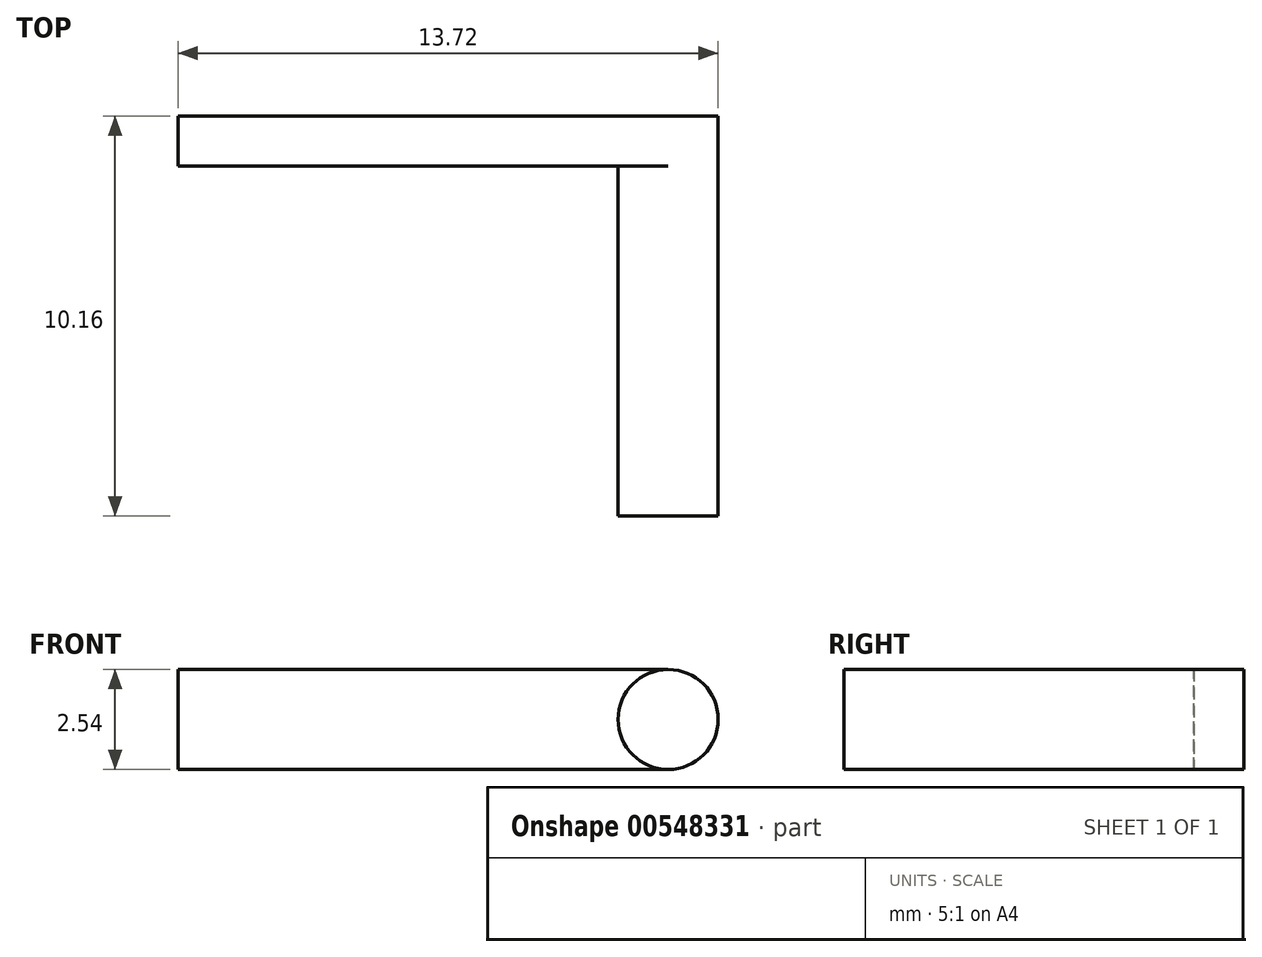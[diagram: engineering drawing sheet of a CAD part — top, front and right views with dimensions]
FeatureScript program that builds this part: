
annotation { "Feature Type Name" : "Feature", "Feature Type Description" : "" }
export const myFeature = defineFeature(function(context is Context, id is Id, definition is map)
    precondition{}
    {
        {
            var Q0;
            Q0=qCreatedBy(makeId("Front.planeOp"),FACE);
            var sketch = newSketch(context, id + "F0", { "sketchPlane" : qUnion([Q0])});
            skCircle(sketch, "E0", {"center": v(0, 0) * mm, "radius": 1.27 * mm});
            skLineSegment(sketch, "E1", {"start": v(0, -1.27) * mm, "end": v(-12.45, -1.27) * mm});
            skLineSegment(sketch, "E2", {"start": v(-12.45, -1.27) * mm, "end": v(-12.45, 0) * mm});
            skLineSegment(sketch, "E3.MirrorCS", {"start": v(0, 1.27) * mm, "end": v(-12.45, 1.27) * mm});
            skLineSegment(sketch, "E4.MirrorCS", {"start": v(-12.45, 1.27) * mm, "end": v(-12.45, 0) * mm});
            skSolve(sketch);
        }
        {
            var Q0;
            {var subQ0=sQuery(id+"F0.wireOp",EDGE,"E0");var subQ1=makeQuery(id+"F0.imprint","INTERSECT",VERTEX,{"derivedFrom":[subQ0,sQuery(id+"F0.wireOp",EDGE,"E1")]});Q0=makeQuery(id+"F0.imprint","IMPRINT",FACE,{"disambiguationData":[TD([[makeQuery(id+"F0.imprint","IMPRINT",EDGE,{"disambiguationData":[TD([[subQ1,1.0]])],"derivedFrom":subQ0}),1.0]])]});}
            extrude(context, id + "F1", {"entities" : qUnion([Q0]), "depth" : 10.16 * mm, "offsetDistance" : 25.4 * mm});
        }
        {
            var Q0;
            {var subQ1=sQuery(id+"F0.wireOp",EDGE,"E1");Q0=makeQuery(id+"F0.imprint","IMPRINT",FACE,{"disambiguationData":[TD([[makeQuery(id+"F0.imprint","IMPRINT",EDGE,{"derivedFrom":subQ1}),-1.0]])]});}
            extrude(context, id + "F2", {"entities" : qUnion([Q0]), "operationType" : NewBodyOperationType.ADD, "depth" : 1.27 * mm, "offsetDistance" : 25.4 * mm});
        }
    });
